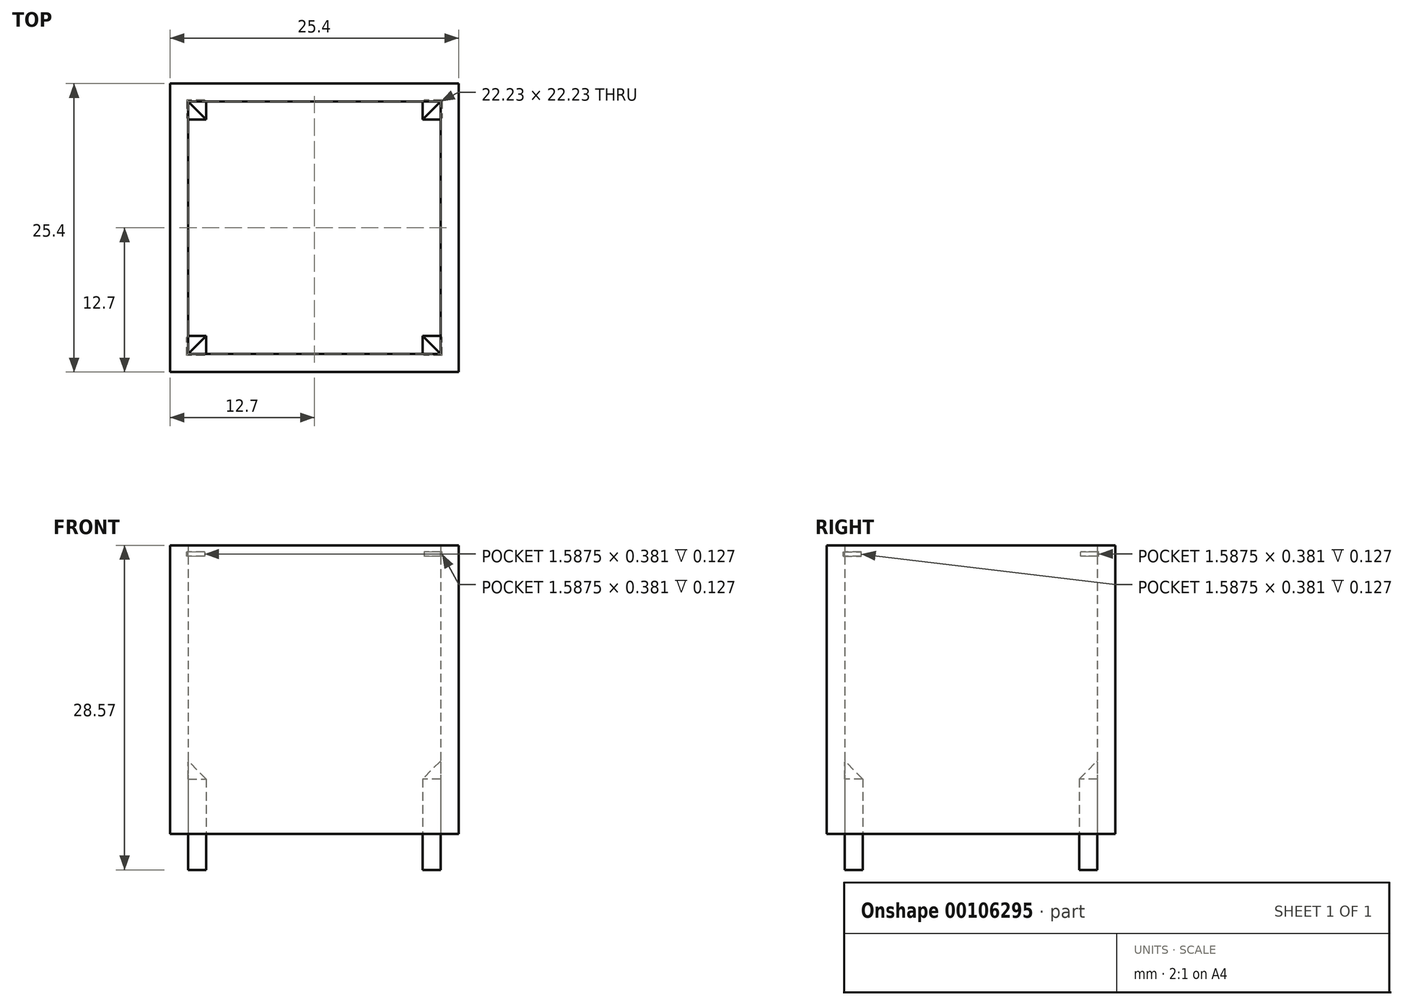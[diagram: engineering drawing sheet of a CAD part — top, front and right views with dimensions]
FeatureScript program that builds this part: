
annotation { "Feature Type Name" : "Feature", "Feature Type Description" : "" }
export const myFeature = defineFeature(function(context is Context, id is Id, definition is map)
    precondition{}
    {
        {
            var Q0;
            Q0=qCreatedBy(makeId("Top.planeOp"),FACE);
            var sketch = newSketch(context, id + "F0", { "sketchPlane" : qUnion([Q0])});
            skLineSegment(sketch, "E0.bottom", {"start": v(12.7, 12.7) * mm, "end": v(-12.7, 12.7) * mm});
            skLineSegment(sketch, "E0.top", {"start": v(12.7, -12.7) * mm, "end": v(-12.7, -12.7) * mm});
            skLineSegment(sketch, "E0.left", {"start": v(12.7, 12.7) * mm, "end": v(12.7, -12.7) * mm});
            skLineSegment(sketch, "E0.right", {"start": v(-12.7, 12.7) * mm, "end": v(-12.7, -12.7) * mm});
            skPoint(sketch, "E0.middle", {"position": v(0, 0) * mm});
            skLineSegment(sketch, "E1.0", {"start": v(11.11, 11.11) * mm, "end": v(-11.11, 11.11) * mm});
            skLineSegment(sketch, "E1.1", {"start": v(11.11, 11.11) * mm, "end": v(11.11, -11.11) * mm});
            skLineSegment(sketch, "E1.2", {"start": v(11.11, -11.11) * mm, "end": v(-11.11, -11.11) * mm});
            skLineSegment(sketch, "E1.3", {"start": v(-11.11, 11.11) * mm, "end": v(-11.11, -11.11) * mm});
            skSolve(sketch);
        }
        {
            var Q0;
            Q0=makeQuery(id+"F0.imprint","IMPRINT",FACE,{"disambiguationData":[TD([[makeQuery(id+"F0.imprint","IMPRINT",EDGE,{"derivedFrom":sQuery(id+"F0.wireOp",EDGE,"E0.bottom")}),1.0]])]});
            extrude(context, id + "F1", {"entities" : qUnion([Q0]), "depth" : 25.4 * mm});
        }
        {
            var Q0;
            Q0=makeQuery(id+"F1.opExtrude","CAP_FACE",FACE,{"disambiguationData":[OSD([sQuery(id+"F0.wireOp",EDGE,"E0.bottom"),sQuery(id+"F0.wireOp",EDGE,"E0.top"),sQuery(id+"F0.wireOp",EDGE,"E0.left"),sQuery(id+"F0.wireOp",EDGE,"E0.right"),sQuery(id+"F0.wireOp",EDGE,"E1.0"),sQuery(id+"F0.wireOp",EDGE,"E1.1"),sQuery(id+"F0.wireOp",EDGE,"E1.2"),sQuery(id+"F0.wireOp",EDGE,"E1.3")])],"isStart":true});
            var sketch = newSketch(context, id + "F2", { "sketchPlane" : qUnion([Q0])});
            skLineSegment(sketch, "E2.0", {"start": v(-9.53, -11.11) * mm, "end": v(-9.53, 11.11) * mm});
            skLineSegment(sketch, "E3.0", {"start": v(11.11, -9.53) * mm, "end": v(-11.11, -9.53) * mm});
            skLineSegment(sketch, "E4.0", {"start": v(9.53, -11.11) * mm, "end": v(9.53, 11.11) * mm});
            skLineSegment(sketch, "E5.0", {"start": v(11.11, 9.53) * mm, "end": v(-11.11, 9.53) * mm});
            skSolve(sketch);
        }
        {
            var Q0;
            {var subQ0=sQuery(id+"F2.wireOp",EDGE,"E2.0");var subQ1=makeQuery(id+"F1.opExtrude","CAP_EDGE",EDGE,{"disambiguationData":[OSD([sQuery(id+"F0.wireOp",EDGE,"E1.0")])],"isStart":true});var subQ2=makeQuery(id+"F2.imprint","INTERSECT",VERTEX,{"derivedFrom":[subQ1,subQ0]});Q0=makeQuery(id+"F2.imprint","IMPRINT",FACE,{"disambiguationData":[TD([[makeQuery(id+"F2.imprint","IMPRINT",EDGE,{"disambiguationData":[TD([[subQ2,-1.0]])],"derivedFrom":subQ0}),1.0]])]});}
            var Q1;
            {var subQ0=sQuery(id+"F2.wireOp",EDGE,"E3.0");var subQ1=makeQuery(id+"F1.opExtrude","CAP_EDGE",EDGE,{"disambiguationData":[OSD([sQuery(id+"F0.wireOp",EDGE,"E1.1")])],"isStart":true});var subQ2=makeQuery(id+"F2.imprint","INTERSECT",VERTEX,{"derivedFrom":[subQ1,subQ0]});Q1=makeQuery(id+"F2.imprint","IMPRINT",FACE,{"disambiguationData":[TD([[makeQuery(id+"F2.imprint","IMPRINT",EDGE,{"disambiguationData":[TD([[subQ2,-1.0]])],"derivedFrom":subQ0}),1.0]])]});}
            var Q2;
            {var subQ0=sQuery(id+"F2.wireOp",EDGE,"E4.0");var subQ1=makeQuery(id+"F1.opExtrude","CAP_EDGE",EDGE,{"disambiguationData":[OSD([sQuery(id+"F0.wireOp",EDGE,"E1.2")])],"isStart":true});var subQ2=makeQuery(id+"F2.imprint","INTERSECT",VERTEX,{"derivedFrom":[subQ1,subQ0]});Q2=makeQuery(id+"F2.imprint","IMPRINT",FACE,{"disambiguationData":[TD([[makeQuery(id+"F2.imprint","IMPRINT",EDGE,{"disambiguationData":[TD([[subQ2,1.0]])],"derivedFrom":subQ0}),-1.0]])]});}
            var Q3;
            {var subQ0=sQuery(id+"F2.wireOp",EDGE,"E2.0");var subQ1=makeQuery(id+"F1.opExtrude","CAP_EDGE",EDGE,{"disambiguationData":[OSD([sQuery(id+"F0.wireOp",EDGE,"E1.2")])],"isStart":true});var subQ2=makeQuery(id+"F2.imprint","INTERSECT",VERTEX,{"derivedFrom":[subQ1,subQ0]});Q3=makeQuery(id+"F2.imprint","IMPRINT",FACE,{"disambiguationData":[TD([[makeQuery(id+"F2.imprint","IMPRINT",EDGE,{"disambiguationData":[TD([[subQ2,1.0]])],"derivedFrom":subQ0}),1.0]])]});}
            extrude(context, id + "F3", {"entities" : qUnion([Q0, Q1, Q2, Q3]), "depth" : 3.17 * mm});
        }
        {
            var Q0;
            Q0=makeQuery(id+"F3.opExtrude","CAP_FACE",FACE,{"disambiguationData":[OSD([sQuery(id+"F0.wireOp",EDGE,"E1.2"),sQuery(id+"F0.wireOp",EDGE,"E1.3"),sQuery(id+"F2.wireOp",EDGE,"E2.0"),sQuery(id+"F2.wireOp",EDGE,"E5.0")])],"isStart":true});
            var Q1;
            Q1=makeQuery(id+"F3.opExtrude","CAP_FACE",FACE,{"disambiguationData":[OSD([sQuery(id+"F0.wireOp",EDGE,"E1.0"),sQuery(id+"F0.wireOp",EDGE,"E1.3"),sQuery(id+"F2.wireOp",EDGE,"E2.0"),sQuery(id+"F2.wireOp",EDGE,"E3.0")])],"isStart":true});
            var Q2;
            Q2=makeQuery(id+"F3.opExtrude","CAP_FACE",FACE,{"disambiguationData":[OSD([sQuery(id+"F0.wireOp",EDGE,"E1.0"),sQuery(id+"F0.wireOp",EDGE,"E1.1"),sQuery(id+"F2.wireOp",EDGE,"E3.0"),sQuery(id+"F2.wireOp",EDGE,"E4.0")])],"isStart":true});
            var Q3;
            Q3=makeQuery(id+"F3.opExtrude","CAP_FACE",FACE,{"disambiguationData":[OSD([sQuery(id+"F0.wireOp",EDGE,"E1.1"),sQuery(id+"F0.wireOp",EDGE,"E1.2"),sQuery(id+"F2.wireOp",EDGE,"E4.0"),sQuery(id+"F2.wireOp",EDGE,"E5.0")])],"isStart":true});
            extrude(context, id + "F4", {"entities" : qUnion([Q0, Q1, Q2, Q3]), "depth" : 6.35 * mm});
        }
        {
            var Q0;
            {var subQ0=sQuery(id+"F2.wireOp",EDGE,"E5.0");Q0=makeQuery(id+"F4.opExtrude","CAP_EDGE",EDGE,{"disambiguationData":[OSD([subQ0]),TDD([makeQuery(id+"F3.opExtrude","CAP_EDGE",EDGE,{"disambiguationData":[OSD([subQ0]),TDD([makeQuery(id+"F2.imprint","IMPRINT",EDGE,{"disambiguationData":[TD([[makeQuery(id+"F2.imprint","INTERSECT",VERTEX,{"derivedFrom":[makeQuery(id+"F1.opExtrude","CAP_EDGE",EDGE,{"disambiguationData":[OSD([sQuery(id+"F0.wireOp",EDGE,"E1.1")])],"isStart":true}),subQ0]}),-1.0]])],"derivedFrom":subQ0})])],"isStart":true})])],"isStart":false});}
            var Q1;
            {var subQ0=sQuery(id+"F2.wireOp",EDGE,"E4.0");Q1=makeQuery(id+"F4.opExtrude","CAP_EDGE",EDGE,{"disambiguationData":[OSD([subQ0]),TDD([makeQuery(id+"F3.opExtrude","CAP_EDGE",EDGE,{"disambiguationData":[OSD([subQ0]),TDD([makeQuery(id+"F2.imprint","IMPRINT",EDGE,{"disambiguationData":[TD([[makeQuery(id+"F2.imprint","INTERSECT",VERTEX,{"derivedFrom":[makeQuery(id+"F1.opExtrude","CAP_EDGE",EDGE,{"disambiguationData":[OSD([sQuery(id+"F0.wireOp",EDGE,"E1.2")])],"isStart":true}),subQ0]}),1.0]])],"derivedFrom":subQ0})])],"isStart":true})])],"isStart":false});}
            var Q2;
            {var subQ0=sQuery(id+"F2.wireOp",EDGE,"E3.0");Q2=makeQuery(id+"F4.opExtrude","CAP_EDGE",EDGE,{"disambiguationData":[OSD([subQ0]),TDD([makeQuery(id+"F3.opExtrude","CAP_EDGE",EDGE,{"disambiguationData":[OSD([subQ0]),TDD([makeQuery(id+"F2.imprint","IMPRINT",EDGE,{"disambiguationData":[TD([[makeQuery(id+"F2.imprint","INTERSECT",VERTEX,{"derivedFrom":[makeQuery(id+"F1.opExtrude","CAP_EDGE",EDGE,{"disambiguationData":[OSD([sQuery(id+"F0.wireOp",EDGE,"E1.1")])],"isStart":true}),subQ0]}),-1.0]])],"derivedFrom":subQ0})])],"isStart":true})])],"isStart":false});}
            var Q3;
            {var subQ0=sQuery(id+"F2.wireOp",EDGE,"E4.0");Q3=makeQuery(id+"F4.opExtrude","CAP_EDGE",EDGE,{"disambiguationData":[OSD([subQ0]),TDD([makeQuery(id+"F3.opExtrude","CAP_EDGE",EDGE,{"disambiguationData":[OSD([subQ0]),TDD([makeQuery(id+"F2.imprint","IMPRINT",EDGE,{"disambiguationData":[TD([[makeQuery(id+"F2.imprint","INTERSECT",VERTEX,{"derivedFrom":[makeQuery(id+"F1.opExtrude","CAP_EDGE",EDGE,{"disambiguationData":[OSD([sQuery(id+"F0.wireOp",EDGE,"E1.0")])],"isStart":true}),subQ0]}),-1.0]])],"derivedFrom":subQ0})])],"isStart":true})])],"isStart":false});}
            var Q4;
            {var subQ0=sQuery(id+"F2.wireOp",EDGE,"E3.0");Q4=makeQuery(id+"F4.opExtrude","CAP_EDGE",EDGE,{"disambiguationData":[OSD([subQ0]),TDD([makeQuery(id+"F3.opExtrude","CAP_EDGE",EDGE,{"disambiguationData":[OSD([subQ0]),TDD([makeQuery(id+"F2.imprint","IMPRINT",EDGE,{"disambiguationData":[TD([[makeQuery(id+"F2.imprint","INTERSECT",VERTEX,{"derivedFrom":[makeQuery(id+"F1.opExtrude","CAP_EDGE",EDGE,{"disambiguationData":[OSD([sQuery(id+"F0.wireOp",EDGE,"E1.3")])],"isStart":true}),subQ0]}),1.0]])],"derivedFrom":subQ0})])],"isStart":true})])],"isStart":false});}
            var Q5;
            {var subQ0=sQuery(id+"F2.wireOp",EDGE,"E2.0");Q5=makeQuery(id+"F4.opExtrude","CAP_EDGE",EDGE,{"disambiguationData":[OSD([subQ0]),TDD([makeQuery(id+"F3.opExtrude","CAP_EDGE",EDGE,{"disambiguationData":[OSD([subQ0]),TDD([makeQuery(id+"F2.imprint","IMPRINT",EDGE,{"disambiguationData":[TD([[makeQuery(id+"F2.imprint","INTERSECT",VERTEX,{"derivedFrom":[makeQuery(id+"F1.opExtrude","CAP_EDGE",EDGE,{"disambiguationData":[OSD([sQuery(id+"F0.wireOp",EDGE,"E1.0")])],"isStart":true}),subQ0]}),-1.0]])],"derivedFrom":subQ0})])],"isStart":true})])],"isStart":false});}
            var Q6;
            {var subQ0=sQuery(id+"F2.wireOp",EDGE,"E2.0");Q6=makeQuery(id+"F4.opExtrude","CAP_EDGE",EDGE,{"disambiguationData":[OSD([subQ0]),TDD([makeQuery(id+"F3.opExtrude","CAP_EDGE",EDGE,{"disambiguationData":[OSD([subQ0]),TDD([makeQuery(id+"F2.imprint","IMPRINT",EDGE,{"disambiguationData":[TD([[makeQuery(id+"F2.imprint","INTERSECT",VERTEX,{"derivedFrom":[makeQuery(id+"F1.opExtrude","CAP_EDGE",EDGE,{"disambiguationData":[OSD([sQuery(id+"F0.wireOp",EDGE,"E1.2")])],"isStart":true}),subQ0]}),1.0]])],"derivedFrom":subQ0})])],"isStart":true})])],"isStart":false});}
            var Q7;
            {var subQ0=sQuery(id+"F2.wireOp",EDGE,"E5.0");Q7=makeQuery(id+"F4.opExtrude","CAP_EDGE",EDGE,{"disambiguationData":[OSD([subQ0]),TDD([makeQuery(id+"F3.opExtrude","CAP_EDGE",EDGE,{"disambiguationData":[OSD([subQ0]),TDD([makeQuery(id+"F2.imprint","IMPRINT",EDGE,{"disambiguationData":[TD([[makeQuery(id+"F2.imprint","INTERSECT",VERTEX,{"derivedFrom":[makeQuery(id+"F1.opExtrude","CAP_EDGE",EDGE,{"disambiguationData":[OSD([sQuery(id+"F0.wireOp",EDGE,"E1.3")])],"isStart":true}),subQ0]}),1.0]])],"derivedFrom":subQ0})])],"isStart":true})])],"isStart":false});}
            chamfer(context, id + "F5", {"entities" : qUnion([Q0, Q1, Q2, Q3, Q4, Q5, Q6, Q7]), "width" : 1.52 * mm, "tangentPropagation" : true});
        }
        {
            var Q0;
            Q0=makeQuery(id+"F1.opExtrude","CAP_FACE",FACE,{"disambiguationData":[OSD([sQuery(id+"F0.wireOp",EDGE,"E0.bottom"),sQuery(id+"F0.wireOp",EDGE,"E0.top"),sQuery(id+"F0.wireOp",EDGE,"E0.left"),sQuery(id+"F0.wireOp",EDGE,"E0.right"),sQuery(id+"F0.wireOp",EDGE,"E1.0"),sQuery(id+"F0.wireOp",EDGE,"E1.1"),sQuery(id+"F0.wireOp",EDGE,"E1.2"),sQuery(id+"F0.wireOp",EDGE,"E1.3")])],"isStart":false});
            cPlane(context, id + "F6", {"entities" : qUnion([Q0]), "cplaneType" : CPlaneType.OFFSET, "offset" : 0.76 * mm, "oppositeDirection" : true, "width" : 152.4 * mm, "height" : 152.4 * mm});
        }
        {
            var Q0;
            Q0=qCreatedBy(id+"F6.planeOp",FACE);
            var sketch = newSketch(context, id + "F7", { "sketchPlane" : qUnion([Q0])});
            skPoint(sketch, "E6", {"position": v(-10.45, 10.45) * mm});
            skLineSegment(sketch, "E7.bottom", {"start": v(-9.65, 11.24) * mm, "end": v(-11.24, 11.24) * mm});
            skLineSegment(sketch, "E7.top", {"start": v(-9.65, 9.65) * mm, "end": v(-11.24, 9.65) * mm});
            skLineSegment(sketch, "E7.left", {"start": v(-9.65, 11.24) * mm, "end": v(-9.65, 9.65) * mm});
            skLineSegment(sketch, "E7.right", {"start": v(-11.24, 11.24) * mm, "end": v(-11.24, 9.65) * mm});
            skLineSegment(sketch, "E8.1.0.0", {"start": v(11.24, 11.24) * mm, "end": v(11.24, 9.65) * mm});
            skLineSegment(sketch, "E8.1.0.1", {"start": v(11.24, 11.24) * mm, "end": v(9.65, 11.24) * mm});
            skLineSegment(sketch, "E8.1.0.2", {"start": v(9.65, 11.24) * mm, "end": v(9.65, 9.65) * mm});
            skLineSegment(sketch, "E8.1.0.3", {"start": v(11.24, 9.65) * mm, "end": v(9.65, 9.65) * mm});
            skLineSegment(sketch, "E9.MirrorCS", {"start": v(9.65, -11.24) * mm, "end": v(9.65, -9.65) * mm});
            skLineSegment(sketch, "E10.MirrorCS", {"start": v(11.24, -9.65) * mm, "end": v(9.65, -9.65) * mm});
            skLineSegment(sketch, "E11.MirrorCS", {"start": v(11.24, -11.24) * mm, "end": v(11.24, -9.65) * mm});
            skLineSegment(sketch, "E12.MirrorCS", {"start": v(11.24, -11.24) * mm, "end": v(9.65, -11.24) * mm});
            skLineSegment(sketch, "E13.MirrorCS", {"start": v(-9.65, -9.65) * mm, "end": v(-11.24, -9.65) * mm});
            skLineSegment(sketch, "E14.MirrorCS", {"start": v(-9.65, -11.24) * mm, "end": v(-9.65, -9.65) * mm});
            skLineSegment(sketch, "E15.MirrorCS", {"start": v(-9.65, -11.24) * mm, "end": v(-11.24, -11.24) * mm});
            skLineSegment(sketch, "E16.MirrorCS", {"start": v(-11.24, -11.24) * mm, "end": v(-11.24, -9.65) * mm});
            skSolve(sketch);
        }
        {
            var Q0;
            Q0=makeQuery(id+"F7.imprint","IMPRINT",FACE,{"disambiguationData":[TD([[makeQuery(id+"F7.imprint","IMPRINT",EDGE,{"derivedFrom":sQuery(id+"F7.wireOp",EDGE,"E7.bottom")}),1.0]])]});
            extrude(context, id + "F8", {"entities" : qUnion([Q0]), "operationType" : NewBodyOperationType.REMOVE, "endBound" : BoundingType.SYMMETRIC, "oppositeDirection" : true, "depth" : 0.13 * mm});
        }
        {
            var Q0;
            Q0 = qSketchRegion(id + "F7", true);
            extrude(context, id + "F9", {"entities" : qUnion([Q0]), "operationType" : NewBodyOperationType.REMOVE, "endBound" : BoundingType.SYMMETRIC, "oppositeDirection" : true, "depth" : 0.38 * mm});
        }
    });
